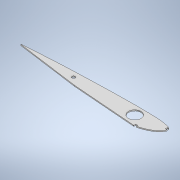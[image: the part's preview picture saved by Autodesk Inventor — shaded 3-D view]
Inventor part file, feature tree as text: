
AUTODESK INVENTOR PART (.ipt)
format: ipt  version: 2022 (Build 260153000, 153)  size: 174,592 bytes
history: native  units: mm
features: extrude x1, sketch x1
ambient origin geometry x8: Origin, YZ Plane, XZ Plane, XY Plane, X Axis, Y Axis, Z Axis, Center Point
bodies: Body1 (feature_tree)
feature tree (2):
  extrude  "Extrusion4"  Depth=160.0mm
  sketch  "Sketch1"  dims[d5=160.0mm d8=160.0mm d17=5.0mm d18=5.0mm d25=6.0mm d26=5.0mm d27=5.0mm d31=34.456mm d36=5.0mm d37=5.0mm d41=23.0mm d50=368.759386mm d60=8.0mm d62=31.0mm d63=2.5mm d64=0.0mm]
